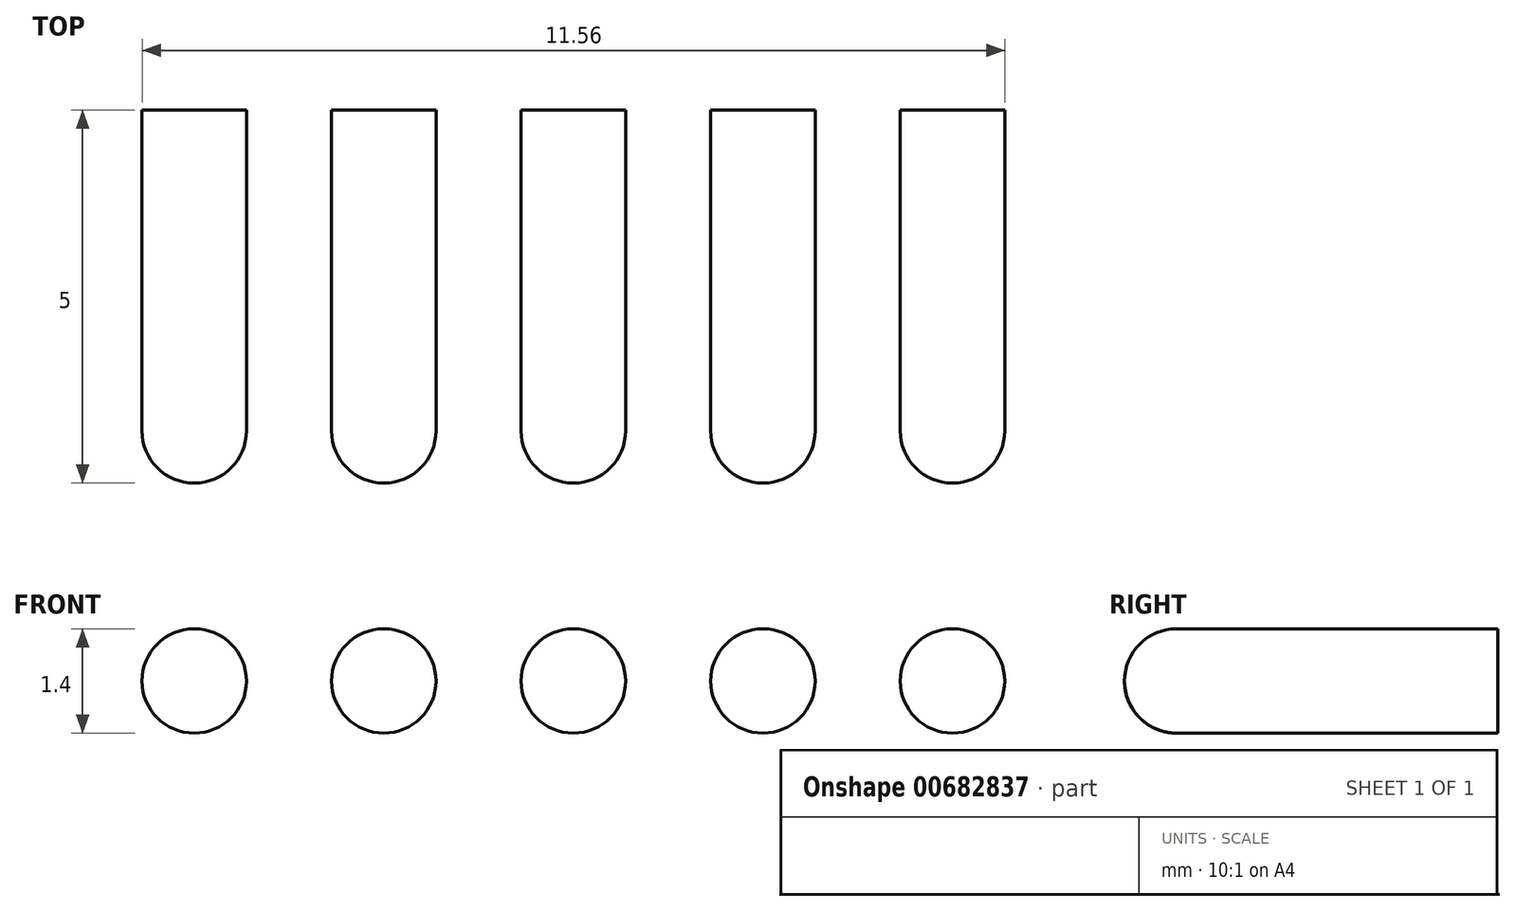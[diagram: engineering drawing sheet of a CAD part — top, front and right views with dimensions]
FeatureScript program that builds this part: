
annotation { "Feature Type Name" : "Feature", "Feature Type Description" : "" }
export const myFeature = defineFeature(function(context is Context, id is Id, definition is map)
    precondition{}
    {
        {
            var Q0;
            Q0=qCreatedBy(makeId("Front.planeOp"),FACE);
            var sketch = newSketch(context, id + "F0", { "sketchPlane" : qUnion([Q0])});
            skCircle(sketch, "E0", {"center": v(-5.72, -0.22) * mm, "radius": 0.7 * mm});
            skCircle(sketch, "E1", {"center": v(-3.18, -0.22) * mm, "radius": 0.7 * mm});
            skCircle(sketch, "E2", {"center": v(-0.64, -0.22) * mm, "radius": 0.7 * mm});
            skCircle(sketch, "E3", {"center": v(1.9, -0.22) * mm, "radius": 0.7 * mm});
            skCircle(sketch, "E4", {"center": v(4.44, -0.22) * mm, "radius": 0.7 * mm});
            skSolve(sketch);
        }
        {
            var Q0;
            Q0 = qSketchRegion(id + "F0", true);
            extrude(context, id + "F1", {"entities" : qUnion([Q0]), "depth" : 5 * mm, "offsetDistance" : 25 * mm});
        }
        {
            var Q0;
            Q0=makeQuery(id+"F1.opExtrude","CAP_EDGE",EDGE,{"disambiguationData":[OSD([sQuery(id+"F0.wireOp",EDGE,"E0")])],"isStart":false});
            var Q1;
            Q1=makeQuery(id+"F1.opExtrude","CAP_EDGE",EDGE,{"disambiguationData":[OSD([sQuery(id+"F0.wireOp",EDGE,"E1")])],"isStart":false});
            var Q2;
            Q2=makeQuery(id+"F1.opExtrude","CAP_EDGE",EDGE,{"disambiguationData":[OSD([sQuery(id+"F0.wireOp",EDGE,"E2")])],"isStart":false});
            var Q3;
            Q3=makeQuery(id+"F1.opExtrude","CAP_EDGE",EDGE,{"disambiguationData":[OSD([sQuery(id+"F0.wireOp",EDGE,"E3")])],"isStart":false});
            var Q4;
            Q4=makeQuery(id+"F1.opExtrude","CAP_EDGE",EDGE,{"disambiguationData":[OSD([sQuery(id+"F0.wireOp",EDGE,"E4")])],"isStart":false});
            fillet(context, id + "F2", {"entities" : qUnion([Q0, Q1, Q2, Q3, Q4]), "radius" : 0.7 * mm, "tangentPropagation" : true, "allowEdgeOverflow" : false});
        }
    });
